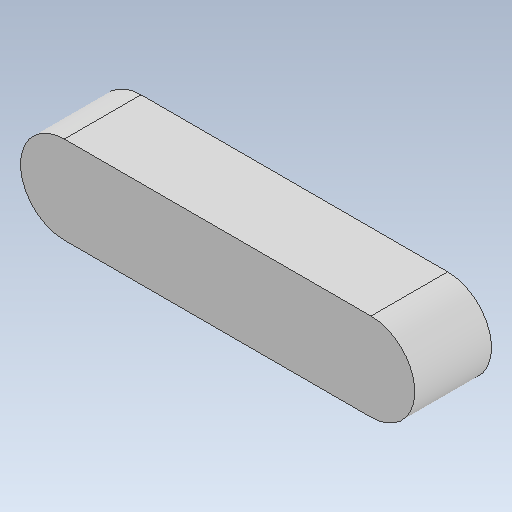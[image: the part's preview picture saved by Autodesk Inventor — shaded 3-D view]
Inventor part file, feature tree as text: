
AUTODESK INVENTOR PART (.ipt)
format: ipt  version: 2020 (Build 240168000, 168)  size: 88,576 bytes
history: native  units: mm
features: other x2, extrude x1, sketch x1, reference x1
ambient origin geometry x8: Origin, YZ Plane, XZ Plane, XY Plane, X Axis, Y Axis, Z Axis, Center Point
bodies: 实体1 (feature_tree)
feature tree (5):
  extrude  "拉伸1"  [1 undecoded]
  sketch  "草图1"  dims[d0=7.0mm d1=0.0mm]
  reference  "参考1"
  other  "<userpath>\Desktop\ME_course_project\课设试试\shaft_try_1.iam"
  other  "shaft_try_1.iam"
note: 1 required parameter value undecoded (feature->parameter linkage not recoverable at this tier; creation-order binding heuristic only, values carry confidence <= 0.55)
